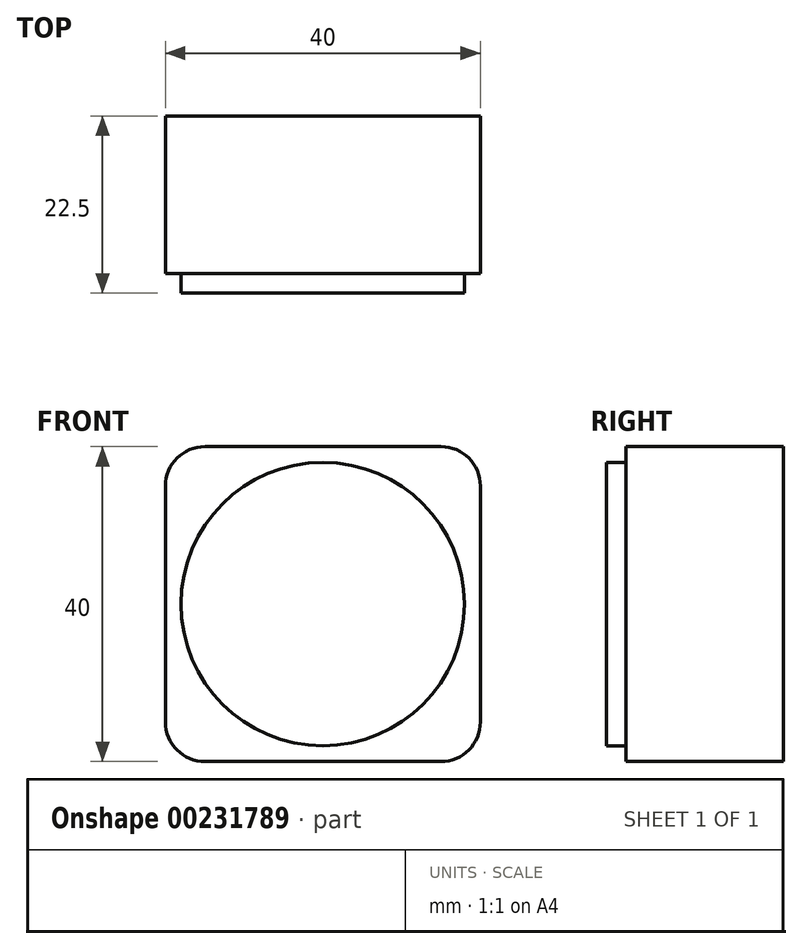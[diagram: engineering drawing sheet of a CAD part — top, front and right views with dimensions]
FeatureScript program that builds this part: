
annotation { "Feature Type Name" : "Feature", "Feature Type Description" : "" }
export const myFeature = defineFeature(function(context is Context, id is Id, definition is map)
    precondition{}
    {
        {
            var Q0;
            Q0=qCreatedBy(makeId("Front.planeOp"),FACE);
            var sketch = newSketch(context, id + "F0", { "sketchPlane" : qUnion([Q0])});
            skLineSegment(sketch, "E0.bottom", {"start": v(0, 0) * mm, "end": v(40, 0) * mm});
            skLineSegment(sketch, "E0.top", {"start": v(0, 40) * mm, "end": v(40, 40) * mm});
            skLineSegment(sketch, "E0.left", {"start": v(0, 0) * mm, "end": v(0, 40) * mm});
            skLineSegment(sketch, "E0.right", {"start": v(40, 0) * mm, "end": v(40, 40) * mm});
            skSolve(sketch);
        }
        {
            var Q0;
            Q0 = qSketchRegion(id + "F0", true);
            extrude(context, id + "F1", {"entities" : qUnion([Q0]), "depth" : 20 * mm});
        }
        {
            var Q0;
            Q0=makeQuery(id+"F1.opExtrude","SWEPT_EDGE",EDGE,{"disambiguationData":[OSD([sQuery(id+"F0.wireOp",EDGE,"E0.top"),sQuery(id+"F0.wireOp",EDGE,"E0.left")])]});
            var Q1;
            Q1=makeQuery(id+"F1.opExtrude","SWEPT_EDGE",EDGE,{"disambiguationData":[OSD([sQuery(id+"F0.wireOp",EDGE,"E0.top"),sQuery(id+"F0.wireOp",EDGE,"E0.right")])]});
            var Q2;
            Q2=makeQuery(id+"F1.opExtrude","SWEPT_EDGE",EDGE,{"disambiguationData":[OSD([sQuery(id+"F0.wireOp",EDGE,"E0.bottom"),sQuery(id+"F0.wireOp",EDGE,"E0.left")])]});
            var Q3;
            Q3=makeQuery(id+"F1.opExtrude","SWEPT_EDGE",EDGE,{"disambiguationData":[OSD([sQuery(id+"F0.wireOp",EDGE,"E0.bottom"),sQuery(id+"F0.wireOp",EDGE,"E0.right")])]});
            fillet(context, id + "F2", {"entities" : qUnion([Q0, Q1, Q2, Q3]), "radius" : 5 * mm, "tangentPropagation" : true, "allowEdgeOverflow" : false});
        }
        {
            var Q0;
            Q0=makeQuery(id+"F1.opExtrude","CAP_FACE",FACE,{"disambiguationData":[OSD([sQuery(id+"F0.wireOp",EDGE,"E0.bottom"),sQuery(id+"F0.wireOp",EDGE,"E0.top"),sQuery(id+"F0.wireOp",EDGE,"E0.left"),sQuery(id+"F0.wireOp",EDGE,"E0.right")])],"isStart":false});
            var sketch = newSketch(context, id + "F3", { "sketchPlane" : qUnion([Q0])});
            skCircle(sketch, "E1", {"center": v(19.98, 20) * mm, "radius": 18 * mm});
            skLineSegment(sketch, "E2", {"start": v(0, 20) * mm, "end": v(40, 20) * mm, "construction": true});
            skLineSegment(sketch, "E3", {"start": v(20, 0) * mm, "end": v(19.98, 20) * mm, "construction": true});
            skSolve(sketch);
        }
        {
            var Q0;
            Q0 = qSketchRegion(id + "F3", true);
            extrude(context, id + "F4", {"entities" : qUnion([Q0]), "operationType" : NewBodyOperationType.ADD, "depth" : 2.5 * mm});
        }
    });
